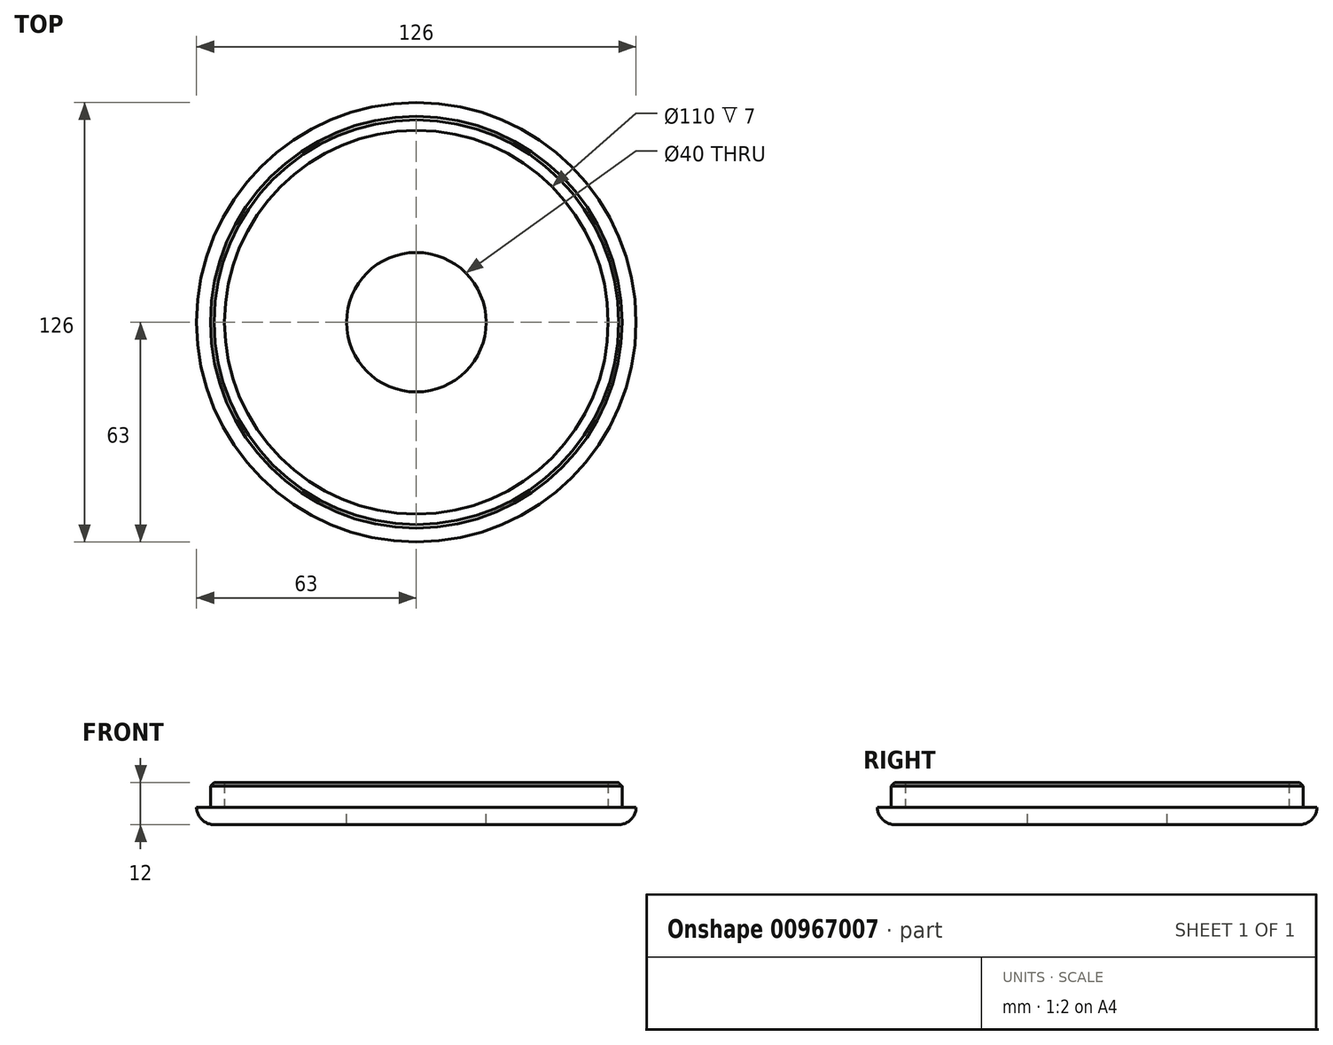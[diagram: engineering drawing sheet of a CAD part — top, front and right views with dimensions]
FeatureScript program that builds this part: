
annotation { "Feature Type Name" : "Feature", "Feature Type Description" : "" }
export const myFeature = defineFeature(function(context is Context, id is Id, definition is map)
    precondition{}
    {
        {
            var Q0;
            Q0=qCreatedBy(makeId("Top.planeOp"),FACE);
            var sketch = newSketch(context, id + "F0", { "sketchPlane" : qUnion([Q0])});
            skCircle(sketch, "E0", {"center": v(0, 0) * mm, "radius": 59 * mm});
            skCircle(sketch, "E1", {"center": v(0, 0) * mm, "radius": 63 * mm});
            skCircle(sketch, "E2", {"center": v(0, 0) * mm, "radius": 55 * mm});
            skCircle(sketch, "E3", {"center": v(0, 0) * mm, "radius": 20 * mm});
            skSolve(sketch);
        }
        {
            var Q0;
            Q0=makeQuery(id+"F0.imprint","IMPRINT",FACE,{"disambiguationData":[TD([[makeQuery(id+"F0.imprint","IMPRINT",EDGE,{"derivedFrom":sQuery(id+"F0.wireOp",EDGE,"E0")}),1.0]])]});
            extrude(context, id + "F1", {"entities" : qUnion([Q0]), "depth" : 7 * mm, "offsetDistance" : 25 * mm});
        }
        {
            var Q0;
            Q0=makeQuery(id+"F0.imprint","IMPRINT",FACE,{"disambiguationData":[TD([[makeQuery(id+"F0.imprint","IMPRINT",EDGE,{"derivedFrom":sQuery(id+"F0.wireOp",EDGE,"E0")}),-1.0]])]});
            var Q1;
            Q1=makeQuery(id+"F0.imprint","IMPRINT",FACE,{"disambiguationData":[TD([[makeQuery(id+"F0.imprint","IMPRINT",EDGE,{"derivedFrom":sQuery(id+"F0.wireOp",EDGE,"E0")}),1.0]])]});
            var Q2;
            Q2=makeQuery(id+"F0.imprint","IMPRINT",FACE,{"disambiguationData":[TD([[makeQuery(id+"F0.imprint","IMPRINT",EDGE,{"derivedFrom":sQuery(id+"F0.wireOp",EDGE,"E2")}),1.0]])]});
            extrude(context, id + "F2", {"entities" : qUnion([Q0, Q1, Q2]), "operationType" : NewBodyOperationType.ADD, "oppositeDirection" : true, "depth" : 5 * mm, "offsetDistance" : 25 * mm});
        }
        {
            var Q0;
            Q0=makeQuery(id+"F2.opExtrude","CAP_EDGE",EDGE,{"disambiguationData":[OSD([sQuery(id+"F0.wireOp",EDGE,"E1")])],"isStart":false});
            fillet(context, id + "F3", {"entities" : qUnion([Q0]), "radius" : 5 * mm, "tangentPropagation" : true, "allowEdgeOverflow" : false});
        }
        {
            var Q0;
            Q0=makeQuery(id+"F1.opExtrude","CAP_EDGE",EDGE,{"disambiguationData":[OSD([sQuery(id+"F0.wireOp",EDGE,"E0")])],"isStart":false});
            chamfer(context, id + "F4", {"entities" : qUnion([Q0]), "width" : 1 * mm, "tangentPropagation" : true});
        }
    });
